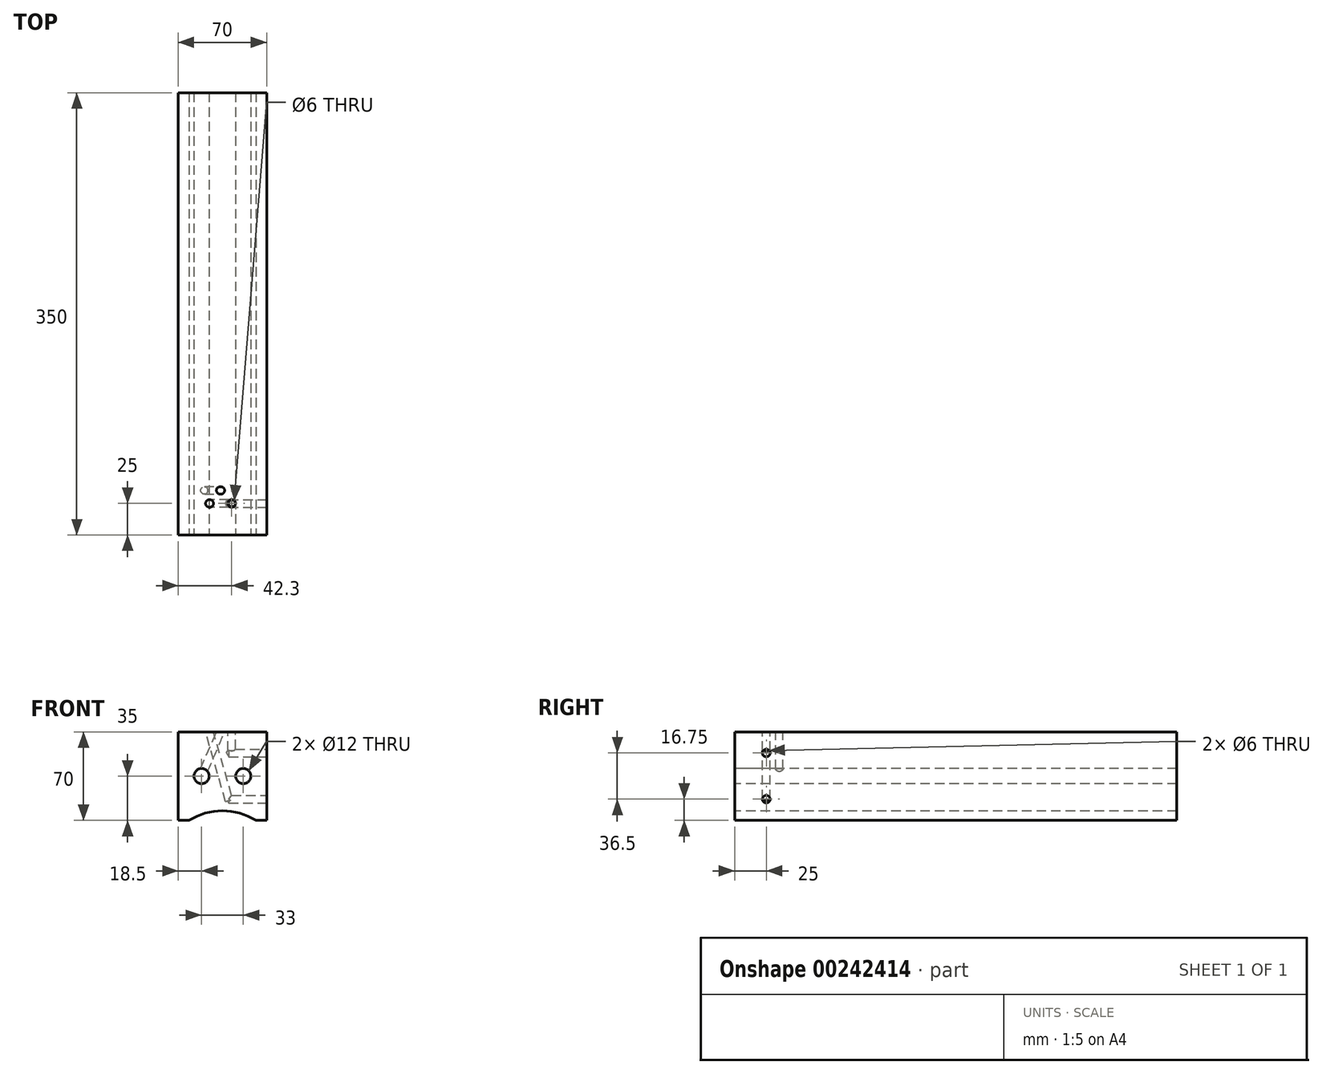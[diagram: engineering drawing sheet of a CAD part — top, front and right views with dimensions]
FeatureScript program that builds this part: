
annotation { "Feature Type Name" : "Feature", "Feature Type Description" : "" }
export const myFeature = defineFeature(function(context is Context, id is Id, definition is map)
    precondition{}
    {
        {
            var Q0;
            Q0=qCreatedBy(makeId("Front.planeOp"),FACE);
            var sketch = newSketch(context, id + "F0", { "sketchPlane" : qUnion([Q0])});
            skLineSegment(sketch, "E0.bottom", {"start": v(0, 0) * mm, "end": v(8.57, 0) * mm});
            skLineSegment(sketch, "E0.top", {"start": v(0, 70) * mm, "end": v(70, 70) * mm});
            skLineSegment(sketch, "E0.left", {"start": v(0, 0) * mm, "end": v(0, 70) * mm});
            skLineSegment(sketch, "E0.right", {"start": v(70, 0) * mm, "end": v(70, 70) * mm});
            skPoint(sketch, "E1", {"position": v(35, 7.5) * mm});
            skPoint(sketch, "E1.positionSnap0", {"position": v(35, 0) * mm});
            skPoint(sketch, "E2", {"position": v(8.57, 0) * mm});
            skPoint(sketch, "E3", {"position": v(61.43, 0) * mm});
            skArc(sketch, "E4", {"start": v(61.43, 0) * mm, "mid": v(35, 7.5) * mm, "end": v(8.57, 0) * mm});
            skLineSegment(sketch, "E5.trimOffspring", {"start": v(61.43, 0) * mm, "end": v(70, 0) * mm});
            skPoint(sketch, "E6", {"position": v(18.5, 35) * mm});
            skPoint(sketch, "E6.positionSnap0", {"position": v(0, 35) * mm});
            skPoint(sketch, "E7", {"position": v(51.5, 35) * mm});
            skCircle(sketch, "E8", {"center": v(18.5, 35) * mm, "radius": 6 * mm});
            skCircle(sketch, "E9", {"center": v(51.5, 35) * mm, "radius": 6 * mm});
            skSolve(sketch);
        }
        {
            var Q0;
            Q0=makeQuery(id+"F0.imprint","IMPRINT",FACE,{"disambiguationData":[TD([[makeQuery(id+"F0.imprint","IMPRINT",EDGE,{"derivedFrom":sQuery(id+"F0.wireOp",EDGE,"E0.bottom")}),1.0]])]});
            extrude(context, id + "F1", {"entities" : qUnion([Q0]), "oppositeDirection" : true, "depth" : 350 * mm});
        }
        {
            var Q0;
            Q0=makeQuery(id+"F1.opExtrude","SWEPT_FACE",FACE,{"disambiguationData":[OSD([sQuery(id+"F0.wireOp",EDGE,"E0.right")])]});
            var sketch = newSketch(context, id + "F2", { "sketchPlane" : qUnion([Q0])});
            skPoint(sketch, "E10", {"position": v(25, 53.25) * mm});
            skPoint(sketch, "E11", {"position": v(25, 16.75) * mm});
            skPoint(sketch, "E12.1.0.0", {"position": v(75, 53.25) * mm});
            skPoint(sketch, "E12.1.0.1", {"position": v(75, 16.75) * mm});
            skPoint(sketch, "E12.2.0.0", {"position": v(125, 53.25) * mm});
            skPoint(sketch, "E12.2.0.1", {"position": v(125, 16.75) * mm});
            skPoint(sketch, "E12.3.0.0", {"position": v(175, 53.25) * mm});
            skPoint(sketch, "E12.3.0.1", {"position": v(175, 16.75) * mm});
            skPoint(sketch, "E12.4.0.0", {"position": v(225, 53.25) * mm});
            skPoint(sketch, "E12.4.0.1", {"position": v(225, 16.75) * mm});
            skPoint(sketch, "E12.5.0.0", {"position": v(275, 53.25) * mm});
            skPoint(sketch, "E12.5.0.1", {"position": v(275, 16.75) * mm});
            skPoint(sketch, "E12.6.0.0", {"position": v(325, 53.25) * mm});
            skPoint(sketch, "E12.6.0.1", {"position": v(325, 16.75) * mm});
            skLineSegment(sketch, "E12.direction1", {"start": v(25, 53.25) * mm, "end": v(75, 53.25) * mm, "construction": true});
            skSolve(sketch);
        }
        {
            var Q0;
            Q0=makeQuery(id+"F1.opExtrude","SWEPT_FACE",FACE,{"disambiguationData":[OSD([sQuery(id+"F0.wireOp",EDGE,"E0.top")])]});
            var sketch = newSketch(context, id + "F3", { "sketchPlane" : qUnion([Q0])});
            skPoint(sketch, "E13", {"position": v(14.5, 8.75) * mm});
            skPoint(sketch, "E14", {"position": v(14.5, 41.25) * mm});
            skPoint(sketch, "E15", {"position": v(55, 40.5) * mm});
            skPoint(sketch, "E16", {"position": v(55, 9.5) * mm});
            skPoint(sketch, "E17", {"position": v(24.8, 25) * mm});
            skPoint(sketch, "E18", {"position": v(42.3, 25) * mm});
            skPoint(sketch, "E19", {"position": v(33.5, 14.7) * mm});
            skPoint(sketch, "E20", {"position": v(33.5, 35.3) * mm});
            skPoint(sketch, "E21", {"position": v(14.5, 61.76) * mm});
            skPoint(sketch, "E22", {"position": v(14.5, 94.26) * mm});
            skPoint(sketch, "E23", {"position": v(55, 62.51) * mm});
            skPoint(sketch, "E24", {"position": v(55, 93.51) * mm});
            skPoint(sketch, "E25", {"position": v(24.8, 78.01) * mm});
            skPoint(sketch, "E26", {"position": v(42.3, 78.01) * mm});
            skPoint(sketch, "E27", {"position": v(33.5, 67.71) * mm});
            skPoint(sketch, "E28", {"position": v(33.5, 88.31) * mm});
            skPoint(sketch, "E29.1.0.0", {"position": v(14.5, 111.76) * mm});
            skPoint(sketch, "E29.1.0.1", {"position": v(55, 112.51) * mm});
            skPoint(sketch, "E29.1.0.2", {"position": v(33.5, 117.71) * mm});
            skPoint(sketch, "E29.1.0.3", {"position": v(42.3, 128.01) * mm});
            skPoint(sketch, "E29.1.0.4", {"position": v(24.8, 128.01) * mm});
            skPoint(sketch, "E29.1.0.5", {"position": v(33.5, 138.31) * mm});
            skPoint(sketch, "E29.1.0.6", {"position": v(55, 143.51) * mm});
            skPoint(sketch, "E29.1.0.7", {"position": v(14.5, 144.26) * mm});
            skPoint(sketch, "E29.2.0.0", {"position": v(14.5, 161.76) * mm});
            skPoint(sketch, "E29.2.0.1", {"position": v(55, 162.51) * mm});
            skPoint(sketch, "E29.2.0.2", {"position": v(33.5, 167.71) * mm});
            skPoint(sketch, "E29.2.0.3", {"position": v(42.3, 178.01) * mm});
            skPoint(sketch, "E29.2.0.4", {"position": v(24.8, 178.01) * mm});
            skPoint(sketch, "E29.2.0.5", {"position": v(33.5, 188.31) * mm});
            skPoint(sketch, "E29.2.0.6", {"position": v(55, 193.51) * mm});
            skPoint(sketch, "E29.2.0.7", {"position": v(14.5, 194.26) * mm});
            skLineSegment(sketch, "E29.direction1", {"start": v(14.5, 61.76) * mm, "end": v(14.5, 111.76) * mm, "construction": true});
            skPoint(sketch, "E30.0.3.0", {"position": v(14.5, 211.76) * mm});
            skPoint(sketch, "E30.1.3.0", {"position": v(55, 212.51) * mm});
            skPoint(sketch, "E30.2.3.0", {"position": v(33.5, 217.71) * mm});
            skPoint(sketch, "E30.3.3.0", {"position": v(42.3, 228.01) * mm});
            skPoint(sketch, "E30.4.3.0", {"position": v(24.8, 228.01) * mm});
            skPoint(sketch, "E30.5.3.0", {"position": v(33.5, 238.31) * mm});
            skPoint(sketch, "E30.6.3.0", {"position": v(55, 243.51) * mm});
            skPoint(sketch, "E30.7.3.0", {"position": v(14.5, 244.26) * mm});
            skPoint(sketch, "E30.0.4.0", {"position": v(14.5, 261.76) * mm});
            skPoint(sketch, "E30.1.4.0", {"position": v(55, 262.51) * mm});
            skPoint(sketch, "E30.2.4.0", {"position": v(33.5, 267.71) * mm});
            skPoint(sketch, "E30.3.4.0", {"position": v(42.3, 278.01) * mm});
            skPoint(sketch, "E30.4.4.0", {"position": v(24.8, 278.01) * mm});
            skPoint(sketch, "E30.5.4.0", {"position": v(33.5, 288.31) * mm});
            skPoint(sketch, "E30.6.4.0", {"position": v(55, 293.51) * mm});
            skPoint(sketch, "E30.7.4.0", {"position": v(14.5, 294.26) * mm});
            skPoint(sketch, "E30.0.5.0", {"position": v(14.5, 311.76) * mm});
            skPoint(sketch, "E30.1.5.0", {"position": v(55, 312.51) * mm});
            skPoint(sketch, "E30.2.5.0", {"position": v(33.5, 317.71) * mm});
            skPoint(sketch, "E30.3.5.0", {"position": v(42.3, 328.01) * mm});
            skPoint(sketch, "E30.4.5.0", {"position": v(24.8, 328.01) * mm});
            skPoint(sketch, "E30.5.5.0", {"position": v(33.5, 338.31) * mm});
            skPoint(sketch, "E30.6.5.0", {"position": v(55, 343.51) * mm});
            skPoint(sketch, "E30.7.5.0", {"position": v(14.5, 344.26) * mm});
            skSolve(sketch);
        }
        {
            var Q0;
            Q0=makeQuery(id+"F1.opExtrude","CAP_FACE",FACE,{"disambiguationData":[OSD([sQuery(id+"F0.wireOp",EDGE,"E0.bottom"),sQuery(id+"F0.wireOp",EDGE,"E0.top"),sQuery(id+"F0.wireOp",EDGE,"E0.left"),sQuery(id+"F0.wireOp",EDGE,"E0.right"),sQuery(id+"F0.wireOp",EDGE,"E4"),sQuery(id+"F0.wireOp",EDGE,"E5.trimOffspring"),sQuery(id+"F0.wireOp",EDGE,"E8"),sQuery(id+"F0.wireOp",EDGE,"E9")])],"isStart":true});
            var Q1;
            Q1=sQuery(id+"F3.wireOp",VERTEX,"E20");
            cPlane(context, id + "F4", {"entities" : qUnion([Q0, Q1]), "cplaneType" : CPlaneType.PLANE_POINT, "offset" : 25 * mm, "width" : 150 * mm, "height" : 150 * mm});
        }
        {
            var Q0;
            Q0=qCreatedBy(id+"F4.planeOp",FACE);
            var sketch = newSketch(context, id + "F5", { "sketchPlane" : qUnion([Q0])});
            skLineSegment(sketch, "E31", {"start": v(34.55, 72.46) * mm, "end": v(18.5, 35) * mm, "construction": true});
            skPoint(sketch, "E32", {"position": v(18.5, 35) * mm});
            skSolve(sketch);
        }
        {
            var Q0;
            Q0=makeQuery(id+"F1.opExtrude","CAP_FACE",FACE,{"disambiguationData":[OSD([sQuery(id+"F0.wireOp",EDGE,"E0.bottom"),sQuery(id+"F0.wireOp",EDGE,"E0.top"),sQuery(id+"F0.wireOp",EDGE,"E0.left"),sQuery(id+"F0.wireOp",EDGE,"E0.right"),sQuery(id+"F0.wireOp",EDGE,"E4"),sQuery(id+"F0.wireOp",EDGE,"E5.trimOffspring"),sQuery(id+"F0.wireOp",EDGE,"E8"),sQuery(id+"F0.wireOp",EDGE,"E9")])],"isStart":true});
            var Q1;
            Q1=sQuery(id+"F3.wireOp",VERTEX,"E18");
            cPlane(context, id + "F6", {"entities" : qUnion([Q0, Q1]), "cplaneType" : CPlaneType.PLANE_POINT, "offset" : 25 * mm, "width" : 150 * mm, "height" : 150 * mm});
        }
        {
            var Q0;
            Q0=sQuery(id+"F2.wireOp",VERTEX,"E10");
            var Q1;
            Q1=makeQuery(id+"F1.opExtrude","SWEPT_BODY",BODY,{"disambiguationData":[OSD([sQuery(id+"F0.wireOp",EDGE,"E0.bottom"),sQuery(id+"F0.wireOp",EDGE,"E0.top"),sQuery(id+"F0.wireOp",EDGE,"E0.left"),sQuery(id+"F0.wireOp",EDGE,"E0.right"),sQuery(id+"F0.wireOp",EDGE,"E4"),sQuery(id+"F0.wireOp",EDGE,"E5.trimOffspring"),sQuery(id+"F0.wireOp",EDGE,"E8"),sQuery(id+"F0.wireOp",EDGE,"E9")])]});
            hole(context, id + "F7", {"style" : HoleStyle.SIMPLE, "endStyle" : HoleEndStyle.BLIND, "holeDiameter" : 6 * mm, "holeDepth" : 30 * mm, "locations" : qUnion([Q0]), "scope" : qUnion([Q1])});
        }
        {
            var Q0;
            Q0=sQuery(id+"F3.wireOp",VERTEX,"E18");
            var Q1;
            Q1=makeQuery(id+"F1.opExtrude","SWEPT_BODY",BODY,{"disambiguationData":[OSD([sQuery(id+"F0.wireOp",EDGE,"E0.bottom"),sQuery(id+"F0.wireOp",EDGE,"E0.top"),sQuery(id+"F0.wireOp",EDGE,"E0.left"),sQuery(id+"F0.wireOp",EDGE,"E0.right"),sQuery(id+"F0.wireOp",EDGE,"E4"),sQuery(id+"F0.wireOp",EDGE,"E5.trimOffspring"),sQuery(id+"F0.wireOp",EDGE,"E8"),sQuery(id+"F0.wireOp",EDGE,"E9")])]});
            hole(context, id + "F8", {"style" : HoleStyle.SIMPLE, "endStyle" : HoleEndStyle.BLIND, "holeDiameter" : 6 * mm, "holeDepth" : 15 * mm, "locations" : qUnion([Q0]), "scope" : qUnion([Q1])});
        }
        {
            var Q0;
            Q0=sQuery(id+"F2.wireOp",VERTEX,"E11");
            var Q1;
            Q1=makeQuery(id+"F1.opExtrude","SWEPT_BODY",BODY,{"disambiguationData":[OSD([sQuery(id+"F0.wireOp",EDGE,"E0.bottom"),sQuery(id+"F0.wireOp",EDGE,"E0.top"),sQuery(id+"F0.wireOp",EDGE,"E0.left"),sQuery(id+"F0.wireOp",EDGE,"E0.right"),sQuery(id+"F0.wireOp",EDGE,"E4"),sQuery(id+"F0.wireOp",EDGE,"E5.trimOffspring"),sQuery(id+"F0.wireOp",EDGE,"E8"),sQuery(id+"F0.wireOp",EDGE,"E9")])]});
            hole(context, id + "F9", {"style" : HoleStyle.SIMPLE, "endStyle" : HoleEndStyle.BLIND, "holeDiameter" : 6 * mm, "holeDepth" : 30 * mm, "locations" : qUnion([Q0]), "scope" : qUnion([Q1])});
        }
        {
            var Q0;
            Q0=qCreatedBy(id+"F6.planeOp",FACE);
            var sketch = newSketch(context, id + "F10", { "sketchPlane" : qUnion([Q0])});
            skLineSegment(sketch, "E33", {"start": v(40, 16.64) * mm, "end": v(23.34, 75.11) * mm});
            skSolve(sketch);
        }
        {
            var Q0;
            Q0=sQuery(id+"F10.wireOp",VERTEX,"E33.end");
            var Q1;
            Q1=sQuery(id+"F10.wireOp",EDGE,"E33");
            cPlane(context, id + "F11", {"entities" : qUnion([Q0, Q1]), "cplaneType" : CPlaneType.LINE_POINT, "offset" : 25 * mm, "width" : 150 * mm, "height" : 150 * mm});
        }
        {
            var Q0;
            Q0=qCreatedBy(id+"F11.planeOp",FACE);
            var sketch = newSketch(context, id + "F12", { "sketchPlane" : qUnion([Q0])});
            skCircle(sketch, "E34", {"center": v(43.03, 25) * mm, "radius": 3 * mm});
            skSolve(sketch);
        }
        {
            var Q0;
            Q0=makeQuery(id+"F12.imprint","IMPRINT",FACE,{"disambiguationData":[TD([[makeQuery(id+"F12.imprint","IMPRINT",EDGE,{"derivedFrom":sQuery(id+"F12.wireOp",EDGE,"E34")}),1.0]])]});
            extrude(context, id + "F13", {"entities" : qUnion([Q0]), "operationType" : NewBodyOperationType.REMOVE, "oppositeDirection" : true, "depth" : 62 * mm});
        }
        {
            var Q0;
            Q0=sQuery(id+"F5.wireOp",VERTEX,"E31.start");
            var Q1;
            Q1=sQuery(id+"F5.wireOp",EDGE,"E31");
            cPlane(context, id + "F14", {"entities" : qUnion([Q0, Q1]), "cplaneType" : CPlaneType.LINE_POINT, "offset" : 25 * mm, "width" : 150 * mm, "height" : 150 * mm});
        }
        {
            var Q0;
            Q0=qCreatedBy(id+"F14.planeOp",FACE);
            var sketch = newSketch(context, id + "F15", { "sketchPlane" : qUnion([Q0])});
            skCircle(sketch, "E35", {"center": v(3.22, -35.3) * mm, "radius": 3 * mm});
            skSolve(sketch);
        }
        {
            var Q0;
            Q0=makeQuery(id+"F15.imprint","IMPRINT",FACE,{"disambiguationData":[TD([[makeQuery(id+"F15.imprint","IMPRINT",EDGE,{"derivedFrom":sQuery(id+"F15.wireOp",EDGE,"E35")}),1.0]])]});
            extrude(context, id + "F16", {"entities" : qUnion([Q0]), "operationType" : NewBodyOperationType.REMOVE, "depth" : 40 * mm});
        }
        {
            var Q0;
            Q0=makeQuery(id+"F1.opExtrude","CAP_FACE",FACE,{"disambiguationData":[OSD([sQuery(id+"F0.wireOp",EDGE,"E0.bottom"),sQuery(id+"F0.wireOp",EDGE,"E0.top"),sQuery(id+"F0.wireOp",EDGE,"E0.left"),sQuery(id+"F0.wireOp",EDGE,"E0.right"),sQuery(id+"F0.wireOp",EDGE,"E4"),sQuery(id+"F0.wireOp",EDGE,"E5.trimOffspring"),sQuery(id+"F0.wireOp",EDGE,"E8"),sQuery(id+"F0.wireOp",EDGE,"E9")])],"isStart":true});
            var Q1;
            Q1=sQuery(id+"F3.wireOp",VERTEX,"E19");
            cPlane(context, id + "F17", {"entities" : qUnion([Q0, Q1]), "cplaneType" : CPlaneType.PLANE_POINT, "offset" : 25 * mm, "width" : 150 * mm, "height" : 150 * mm});
        }
    });
